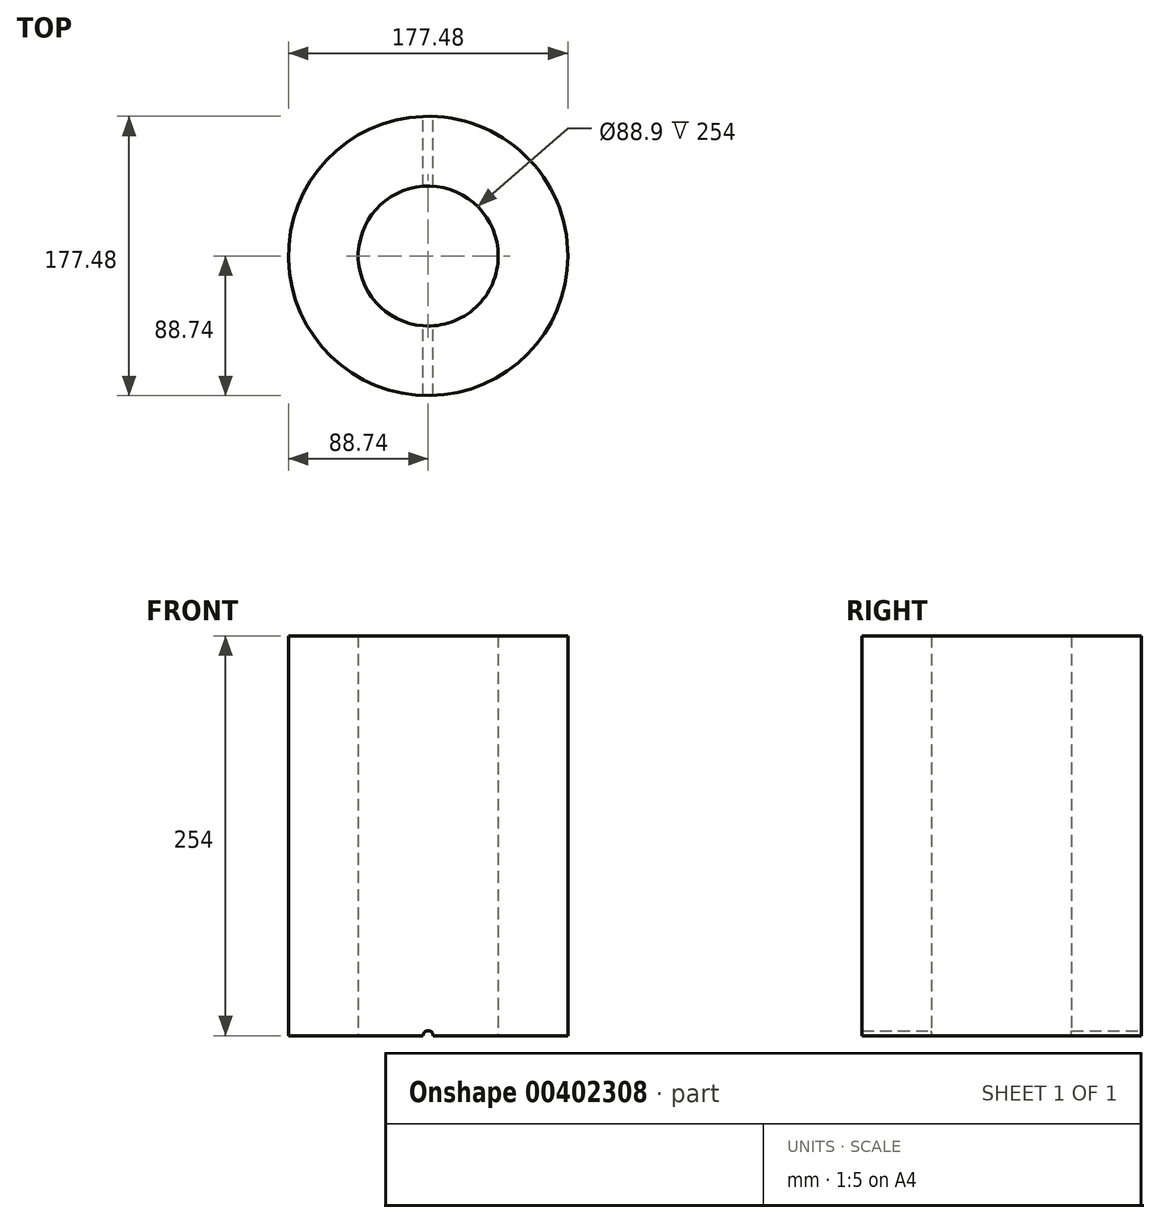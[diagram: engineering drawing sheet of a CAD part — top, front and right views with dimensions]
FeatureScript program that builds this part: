
annotation { "Feature Type Name" : "Feature", "Feature Type Description" : "" }
export const myFeature = defineFeature(function(context is Context, id is Id, definition is map)
    precondition{}
    {
        {
            var Q0;
            Q0=qCreatedBy(makeId("Top.planeOp"),FACE);
            var sketch = newSketch(context, id + "F0", { "sketchPlane" : qUnion([Q0])});
            skCircle(sketch, "E0", {"center": v(0, 0) * mm, "radius": 88.74 * mm});
            skCircle(sketch, "E1", {"center": v(0, 0) * mm, "radius": 44.45 * mm});
            skSolve(sketch);
        }
        {
            var Q0;
            Q0 = qSketchRegion(id + "F0", true);
            extrude(context, id + "F1", {"entities" : qUnion([Q0]), "depth" : 254 * mm});
        }
        {
            var Q0;
            Q0=qCreatedBy(makeId("Front.planeOp"),FACE);
            cPlane(context, id + "F2", {"entities" : qUnion([Q0]), "cplaneType" : CPlaneType.OFFSET, "offset" : 187.38 * mm, "oppositeDirection" : true, "width" : 152.4 * mm, "height" : 152.4 * mm});
        }
        {
            var Q0;
            Q0=qCreatedBy(id+"F2.planeOp",FACE);
            var sketch = newSketch(context, id + "F3", { "sketchPlane" : qUnion([Q0])});
            skCircle(sketch, "E2", {"center": v(0, 0) * mm, "radius": 71.44 * mm});
            skSolve(sketch);
        }
        {
            var Q0;
            Q0=sQuery(id+"F3.wireOp",VERTEX,"E2.center");
            var Q1;
            Q1=makeQuery(id+"F1.opExtrude","SWEPT_BODY",BODY,{"disambiguationData":[OSD([sQuery(id+"F0.wireOp",EDGE,"E0"),sQuery(id+"F0.wireOp",EDGE,"E1")])]});
            hole(context, id + "F4", {"style" : HoleStyle.SIMPLE, "endStyle" : HoleEndStyle.THROUGH, "oppositeDirection" : true, "holeDiameter" : 6.35 * mm, "isTappedThrough" : true, "tappedDepth" : 12.7 * mm, "tapClearance" : 3, "locations" : qUnion([Q0]), "scope" : qUnion([Q1])});
        }
    });
